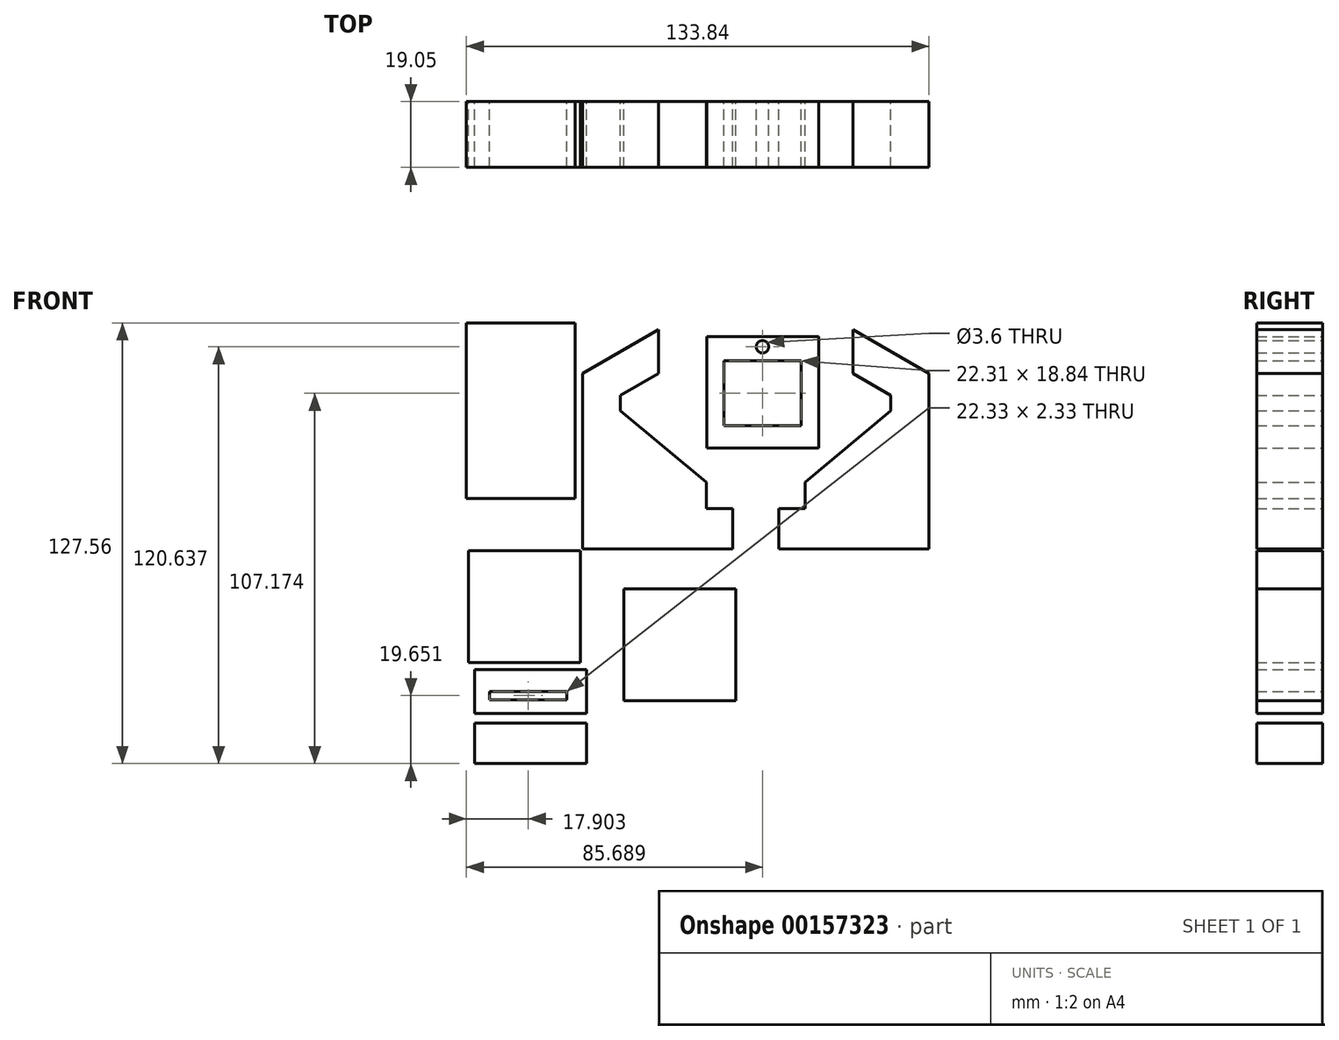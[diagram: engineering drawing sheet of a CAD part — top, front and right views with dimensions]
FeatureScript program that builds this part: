
annotation { "Feature Type Name" : "Feature", "Feature Type Description" : "" }
export const myFeature = defineFeature(function(context is Context, id is Id, definition is map)
    precondition{}
    {
        {
            var Q0;
            Q0=qCreatedBy(makeId("Front.planeOp"),FACE);
            var sketch = newSketch(context, id + "F0", { "sketchPlane" : qUnion([Q0])});
            skLineSegment(sketch, "E0.bottom", {"start": v(-77.07, 77.04) * mm, "end": v(-45.57, 77.04) * mm});
            skLineSegment(sketch, "E0.top", {"start": v(-77.07, 26.24) * mm, "end": v(-45.57, 26.24) * mm});
            skLineSegment(sketch, "E0.left", {"start": v(-77.07, 77.04) * mm, "end": v(-77.07, 26.24) * mm});
            skLineSegment(sketch, "E0.right", {"start": v(-45.57, 77.04) * mm, "end": v(-45.57, 26.24) * mm});
            skLineSegment(sketch, "E1", {"start": v(-21.46, 75.13) * mm, "end": v(-43.46, 62.43) * mm});
            skLineSegment(sketch, "E2", {"start": v(-43.46, 62.43) * mm, "end": v(-43.46, 11.63) * mm});
            skLineSegment(sketch, "E3", {"start": v(-43.46, 11.63) * mm, "end": v(0, 11.63) * mm});
            skLineSegment(sketch, "E4", {"start": v(-21.46, 75.13) * mm, "end": v(-21.46, 62.43) * mm});
            skLineSegment(sketch, "E5", {"start": v(-21.46, 62.43) * mm, "end": v(-32.46, 56.08) * mm});
            skLineSegment(sketch, "E6", {"start": v(-32.46, 56.08) * mm, "end": v(-32.46, 51.64) * mm});
            skPoint(sketch, "E6.endSnap0", {"position": v(-45.57, 51.64) * mm});
            skLineSegment(sketch, "E7", {"start": v(0, 11.63) * mm, "end": v(0, 23.3) * mm});
            skLineSegment(sketch, "E8", {"start": v(0, 23.3) * mm, "end": v(-7.62, 23.3) * mm});
            skLineSegment(sketch, "E9", {"start": v(-7.62, 23.3) * mm, "end": v(-7.62, 30.92) * mm});
            skLineSegment(sketch, "E10", {"start": v(-7.62, 30.92) * mm, "end": v(-32.46, 51.64) * mm});
            skLineSegment(sketch, "E11.MirrorCS", {"start": v(34.77, 75.13) * mm, "end": v(56.77, 62.43) * mm});
            skLineSegment(sketch, "E12.MirrorCS", {"start": v(34.77, 75.13) * mm, "end": v(34.77, 62.43) * mm});
            skLineSegment(sketch, "E13.MirrorCS", {"start": v(34.77, 62.43) * mm, "end": v(45.77, 56.08) * mm});
            skLineSegment(sketch, "E14.MirrorCS", {"start": v(45.77, 56.08) * mm, "end": v(45.77, 51.64) * mm});
            skLineSegment(sketch, "E15.MirrorCS", {"start": v(56.77, 62.43) * mm, "end": v(56.77, 11.63) * mm});
            skLineSegment(sketch, "E16.MirrorCS", {"start": v(20.93, 30.92) * mm, "end": v(45.77, 51.64) * mm});
            skLineSegment(sketch, "E17.MirrorCS", {"start": v(20.93, 23.3) * mm, "end": v(20.93, 30.92) * mm});
            skLineSegment(sketch, "E18.MirrorCS", {"start": v(13.3, 23.3) * mm, "end": v(20.93, 23.3) * mm});
            skLineSegment(sketch, "E19.MirrorCS", {"start": v(13.3, 11.63) * mm, "end": v(13.3, 23.3) * mm});
            skLineSegment(sketch, "E20.MirrorCS", {"start": v(56.77, 11.63) * mm, "end": v(13.3, 11.63) * mm});
            skLineSegment(sketch, "E21.bottom", {"start": v(-7.5, 73.13) * mm, "end": v(24.85, 73.13) * mm});
            skLineSegment(sketch, "E21.top", {"start": v(-7.5, 40.79) * mm, "end": v(24.85, 40.79) * mm});
            skLineSegment(sketch, "E21.left", {"start": v(-7.5, 73.13) * mm, "end": v(-7.5, 40.79) * mm});
            skLineSegment(sketch, "E21.right", {"start": v(24.85, 73.13) * mm, "end": v(24.85, 40.79) * mm});
            skLineSegment(sketch, "E22.bottom", {"start": v(-2.54, 66.08) * mm, "end": v(19.78, 66.08) * mm});
            skLineSegment(sketch, "E22.top", {"start": v(-2.54, 47.23) * mm, "end": v(19.78, 47.23) * mm});
            skLineSegment(sketch, "E22.left", {"start": v(-2.54, 66.08) * mm, "end": v(-2.54, 47.23) * mm});
            skLineSegment(sketch, "E22.right", {"start": v(19.78, 66.08) * mm, "end": v(19.78, 47.23) * mm});
            skLineSegment(sketch, "E23.bottom", {"start": v(-76.42, 11.03) * mm, "end": v(-44.08, 11.03) * mm});
            skLineSegment(sketch, "E23.top", {"start": v(-76.42, -21.31) * mm, "end": v(-44.08, -21.31) * mm});
            skLineSegment(sketch, "E23.left", {"start": v(-76.42, 11.03) * mm, "end": v(-76.42, -21.31) * mm});
            skLineSegment(sketch, "E23.right", {"start": v(-44.08, 11.03) * mm, "end": v(-44.08, -21.31) * mm});
            skLineSegment(sketch, "E24.bottom", {"start": v(-31.47, 0) * mm, "end": v(0.88, 0) * mm});
            skLineSegment(sketch, "E24.top", {"start": v(-31.47, -32.35) * mm, "end": v(0.88, -32.35) * mm});
            skLineSegment(sketch, "E24.left", {"start": v(-31.47, 0) * mm, "end": v(-31.47, -32.35) * mm});
            skLineSegment(sketch, "E24.right", {"start": v(0.88, 0) * mm, "end": v(0.88, -32.35) * mm});
            skLineSegment(sketch, "E25.bottom", {"start": v(-74.69, -23.36) * mm, "end": v(-42.34, -23.36) * mm});
            skLineSegment(sketch, "E25.top", {"start": v(-74.69, -36.06) * mm, "end": v(-42.34, -36.06) * mm});
            skLineSegment(sketch, "E25.left", {"start": v(-74.69, -23.36) * mm, "end": v(-74.69, -36.06) * mm});
            skLineSegment(sketch, "E25.right", {"start": v(-42.34, -23.36) * mm, "end": v(-42.34, -36.06) * mm});
            skPoint(sketch, "E26.firstSnap0", {"position": v(-74.69, -29.7) * mm});
            skLineSegment(sketch, "E26.bottom", {"start": v(-70.33, -29.7) * mm, "end": v(-48, -29.7) * mm});
            skLineSegment(sketch, "E26.top", {"start": v(-70.33, -32.03) * mm, "end": v(-48, -32.03) * mm});
            skLineSegment(sketch, "E26.left", {"start": v(-70.33, -29.7) * mm, "end": v(-70.33, -32.03) * mm});
            skLineSegment(sketch, "E26.right", {"start": v(-48, -29.7) * mm, "end": v(-48, -32.03) * mm});
            skCircle(sketch, "E27", {"center": v(8.62, 70.12) * mm, "radius": 1.8 * mm});
            skPoint(sketch, "E27.centerSnap0", {"position": v(8.62, 66.08) * mm});
            skPoint(sketch, "E28.oppositeSnap0", {"position": v(-42.34, -29.7) * mm});
            skLineSegment(sketch, "E28.bottom", {"start": v(-74.69, -38.85) * mm, "end": v(-42.34, -38.85) * mm});
            skLineSegment(sketch, "E28.top", {"start": v(-74.69, -50.52) * mm, "end": v(-42.34, -50.52) * mm});
            skLineSegment(sketch, "E28.left", {"start": v(-74.69, -38.85) * mm, "end": v(-74.69, -50.52) * mm});
            skLineSegment(sketch, "E28.right", {"start": v(-42.34, -38.85) * mm, "end": v(-42.34, -50.52) * mm});
            skSolve(sketch);
        }
        {
            var Q0;
            Q0 = qSketchRegion(id + "F0", true);
            extrude(context, id + "F1", {"entities" : qUnion([Q0]), "depth" : 19.05 * mm});
        }
    });
